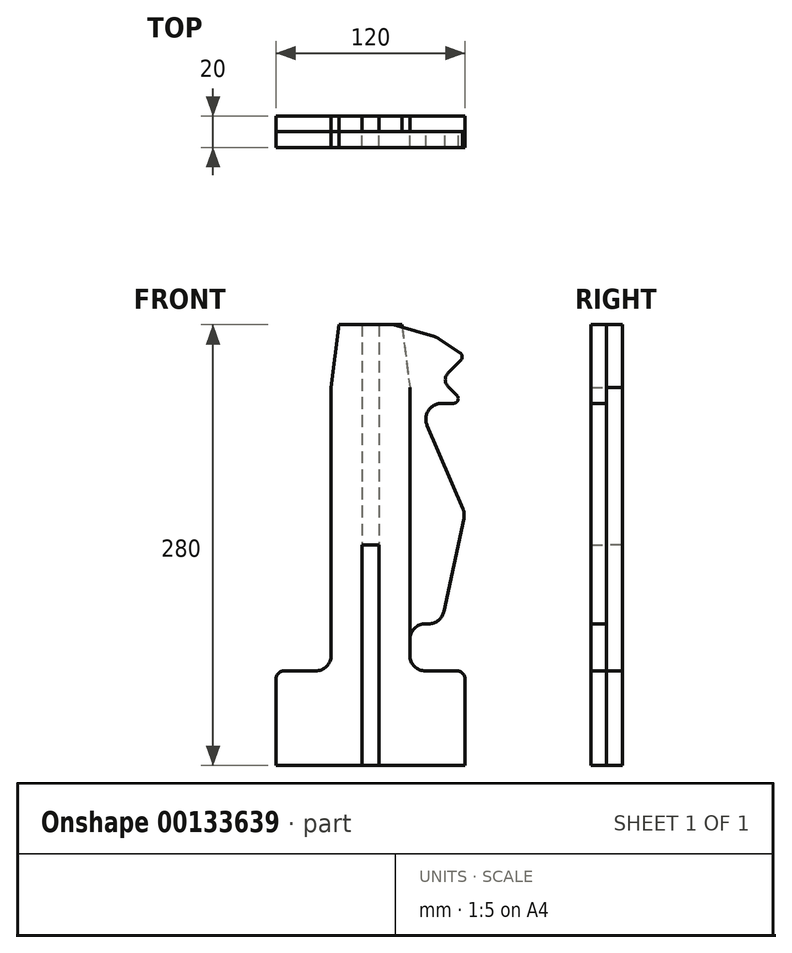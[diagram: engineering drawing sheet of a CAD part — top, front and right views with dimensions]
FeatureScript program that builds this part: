
annotation { "Feature Type Name" : "Feature", "Feature Type Description" : "" }
export const myFeature = defineFeature(function(context is Context, id is Id, definition is map)
    precondition{}
    {
        {
            var Q0;
            Q0=qCreatedBy(makeId("Front.planeOp"),FACE);
            var sketch = newSketch(context, id + "F0", { "sketchPlane" : qUnion([Q0])});
            skLineSegment(sketch, "E0.bottom", {"start": v(55, 30) * mm, "end": v(35, 30) * mm});
            skLineSegment(sketch, "E0.top", {"start": v(60, -30) * mm, "end": v(-60, -30) * mm});
            skLineSegment(sketch, "E0.left", {"start": v(60, 25) * mm, "end": v(60, -30) * mm});
            skLineSegment(sketch, "E0.right", {"start": v(-60, 25) * mm, "end": v(-60, -30) * mm});
            skPoint(sketch, "E0.middle", {"position": v(0, 0) * mm});
            skLineSegment(sketch, "E1", {"start": v(25, 40) * mm, "end": v(25, 50) * mm});
            skLineSegment(sketch, "E2", {"start": v(35, 60) * mm, "end": v(36.92, 60) * mm});
            skLineSegment(sketch, "E3", {"start": v(46.7, 67.9) * mm, "end": v(59.33, 126.89) * mm});
            skLineSegment(sketch, "E4", {"start": v(58.75, 132.92) * mm, "end": v(35.97, 186.06) * mm});
            skLineSegment(sketch, "E5", {"start": v(45.17, 200) * mm, "end": v(52.76, 200) * mm});
            skLineSegment(sketch, "E6", {"start": v(54.88, 205.12) * mm, "end": v(49.24, 210.76) * mm});
            skLineSegment(sketch, "E7", {"start": v(49.24, 219.24) * mm, "end": v(57.41, 227.41) * mm});
            skLineSegment(sketch, "E8", {"start": v(56.96, 232.03) * mm, "end": v(43.26, 241.16) * mm});
            skLineSegment(sketch, "E9", {"start": v(40.55, 242.43) * mm, "end": v(16.4, 249.59) * mm});
            skLineSegment(sketch, "E10", {"start": v(13.55, 250) * mm, "end": v(-23.38, 250) * mm});
            skLineSegment(sketch, "E11", {"start": v(-26.54, 249.49) * mm, "end": v(-40, 245) * mm});
            skLineSegment(sketch, "E12", {"start": v(-40, 245) * mm, "end": v(-55, 253) * mm});
            skLineSegment(sketch, "E13", {"start": v(-55, 253) * mm, "end": v(-50.72, 231.6) * mm});
            skLineSegment(sketch, "E14", {"start": v(-51.79, 224.79) * mm, "end": v(-57.65, 214.23) * mm});
            skLineSegment(sketch, "E15", {"start": v(-58.14, 205.53) * mm, "end": v(-37.44, 155.85) * mm});
            skLineSegment(sketch, "E16", {"start": v(-36.37, 143.82) * mm, "end": v(-52.3, 72.17) * mm});
            skLineSegment(sketch, "E17", {"start": v(-42.53, 60) * mm, "end": v(-35, 60) * mm});
            skLineSegment(sketch, "E18", {"start": v(-25, 50) * mm, "end": v(-25, 40) * mm});
            skPoint(sketch, "E19.visualSharp", {"position": v(-60, 30) * mm});
            skArc(sketch, "E19.filletArc", {"start": v(-55, 30) * mm, "mid": v(-58.54, 28.54) * mm, "end": v(-60, 25) * mm});
            skPoint(sketch, "E20.visualSharp", {"position": v(60, 30) * mm});
            skArc(sketch, "E20.filletArc", {"start": v(60, 25) * mm, "mid": v(58.54, 28.54) * mm, "end": v(55, 30) * mm});
            skPoint(sketch, "E21.visualSharp", {"position": v(-25, 60) * mm});
            skArc(sketch, "E21.filletArc", {"start": v(-25, 50) * mm, "mid": v(-27.93, 57.07) * mm, "end": v(-35, 60) * mm});
            skPoint(sketch, "E22.visualSharp", {"position": v(-55, 60) * mm});
            skArc(sketch, "E22.filletArc", {"start": v(-52.3, 72.17) * mm, "mid": v(-50.33, 63.74) * mm, "end": v(-42.53, 60) * mm});
            skPoint(sketch, "E23.visualSharp", {"position": v(45, 60) * mm});
            skArc(sketch, "E23.filletArc", {"start": v(36.92, 60) * mm, "mid": v(43.2, 62.22) * mm, "end": v(46.7, 67.9) * mm});
            skPoint(sketch, "E24.visualSharp", {"position": v(25, 60) * mm});
            skArc(sketch, "E24.filletArc", {"start": v(35, 60) * mm, "mid": v(27.93, 57.07) * mm, "end": v(25, 50) * mm});
            skPoint(sketch, "E25.newPointA", {"position": v(25, 30) * mm});
            skArc(sketch, "E25.filletArc", {"start": v(25, 40) * mm, "mid": v(27.93, 32.93) * mm, "end": v(35, 30) * mm});
            skLineSegment(sketch, "E26", {"start": v(-55, 30) * mm, "end": v(-35, 30) * mm});
            skPoint(sketch, "E27.visualSharp", {"position": v(-25, 30) * mm});
            skArc(sketch, "E27.filletArc", {"start": v(-35, 30) * mm, "mid": v(-27.93, 32.93) * mm, "end": v(-25, 40) * mm});
            skPoint(sketch, "E28.visualSharp", {"position": v(60, 130) * mm});
            skArc(sketch, "E28.filletArc", {"start": v(59.33, 126.89) * mm, "mid": v(59.5, 129.95) * mm, "end": v(58.75, 132.92) * mm});
            skPoint(sketch, "E29.visualSharp", {"position": v(30, 200) * mm});
            skArc(sketch, "E29.filletArc", {"start": v(45.17, 200) * mm, "mid": v(36.82, 195.5) * mm, "end": v(35.97, 186.06) * mm});
            skPoint(sketch, "E30.visualSharp", {"position": v(60, 200) * mm});
            skArc(sketch, "E30.filletArc", {"start": v(52.76, 200) * mm, "mid": v(55.53, 201.85) * mm, "end": v(54.88, 205.12) * mm});
            skPoint(sketch, "E31.visualSharp", {"position": v(60, 230) * mm});
            skArc(sketch, "E31.filletArc", {"start": v(57.41, 227.41) * mm, "mid": v(58.28, 229.83) * mm, "end": v(56.96, 232.03) * mm});
            skPoint(sketch, "E32.visualSharp", {"position": v(45, 215) * mm});
            skArc(sketch, "E32.filletArc", {"start": v(49.24, 219.24) * mm, "mid": v(47.49, 215) * mm, "end": v(49.24, 210.76) * mm});
            skPoint(sketch, "E33.visualSharp", {"position": v(-35, 150) * mm});
            skArc(sketch, "E33.filletArc", {"start": v(-36.37, 143.82) * mm, "mid": v(-35.98, 149.91) * mm, "end": v(-37.44, 155.85) * mm});
            skPoint(sketch, "E34.visualSharp", {"position": v(-60, 210) * mm});
            skArc(sketch, "E34.filletArc", {"start": v(-57.65, 214.23) * mm, "mid": v(-58.9, 209.94) * mm, "end": v(-58.14, 205.53) * mm});
            skPoint(sketch, "E35.visualSharp", {"position": v(-50, 228) * mm});
            skArc(sketch, "E35.filletArc", {"start": v(-51.79, 224.79) * mm, "mid": v(-50.65, 228.1) * mm, "end": v(-50.72, 231.6) * mm});
            skPoint(sketch, "E36.visualSharp", {"position": v(-25, 250) * mm});
            skArc(sketch, "E36.filletArc", {"start": v(-23.38, 250) * mm, "mid": v(-24.98, 249.87) * mm, "end": v(-26.54, 249.49) * mm});
            skPoint(sketch, "E37.visualSharp", {"position": v(15, 250) * mm});
            skArc(sketch, "E37.filletArc", {"start": v(16.4, 249.59) * mm, "mid": v(14.98, 249.9) * mm, "end": v(13.55, 250) * mm});
            skPoint(sketch, "E38.visualSharp", {"position": v(42, 242) * mm});
            skArc(sketch, "E38.filletArc", {"start": v(43.26, 241.16) * mm, "mid": v(41.95, 241.9) * mm, "end": v(40.55, 242.43) * mm});
            skLineSegment(sketch, "E39.bottom", {"start": v(-5.5, 250) * mm, "end": v(5.5, 250) * mm});
            skLineSegment(sketch, "E39.top", {"start": v(-5.5, 110) * mm, "end": v(5.5, 110) * mm});
            skLineSegment(sketch, "E39.left", {"start": v(-5.5, 250) * mm, "end": v(-5.5, 110) * mm});
            skLineSegment(sketch, "E39.right", {"start": v(5.5, 250) * mm, "end": v(5.5, 110) * mm});
            skPoint(sketch, "E39.middle", {"position": v(0, 180) * mm});
            skLineSegment(sketch, "E40.top", {"start": v(-5.5, -30) * mm, "end": v(5.5, -30) * mm});
            skLineSegment(sketch, "E40.left", {"start": v(-5.5, 110) * mm, "end": v(-5.5, -30) * mm});
            skLineSegment(sketch, "E40.right", {"start": v(5.5, 110) * mm, "end": v(5.5, -30) * mm});
            skPoint(sketch, "E40.middle", {"position": v(0, 40) * mm});
            skLineSegment(sketch, "E41", {"start": v(-25, 40) * mm, "end": v(-25, 210) * mm});
            skLineSegment(sketch, "E42", {"start": v(-25, 210) * mm, "end": v(-20, 250) * mm});
            skLineSegment(sketch, "E43", {"start": v(-20, 250) * mm, "end": v(20, 250) * mm});
            skLineSegment(sketch, "E44", {"start": v(20, 250) * mm, "end": v(25, 210) * mm});
            skLineSegment(sketch, "E45", {"start": v(25, 210) * mm, "end": v(25, 40) * mm});
            skSolve(sketch);
        }
        {
            var Q0;
            Q0=makeQuery(id+"F0.imprint","IMPRINT",FACE,{"disambiguationData":[TD([[makeQuery(id+"F0.imprint","IMPRINT",EDGE,{"derivedFrom":sQuery(id+"F0.wireOp",EDGE,"E2")}),1.0]])]});
            var Q1;
            Q1=makeQuery(id+"F0.imprint","IMPRINT",FACE,{"disambiguationData":[TD([[makeQuery(id+"F0.imprint","IMPRINT",EDGE,{"derivedFrom":sQuery(id+"F0.wireOp",EDGE,"E10")}),1.0]])]});
            var Q2;
            {var subQ6=sQuery(id+"F0.wireOp",EDGE,"E0.right");Q2=makeQuery(id+"F0.imprint","IMPRINT",FACE,{"disambiguationData":[TD([[makeQuery(id+"F0.imprint","IMPRINT",EDGE,{"derivedFrom":subQ6}),1.0]])]});}
            var Q3;
            {var subQ0=sQuery(id+"F0.wireOp",EDGE,"E39.left");Q3=makeQuery(id+"F0.imprint","IMPRINT",FACE,{"disambiguationData":[TD([[makeQuery(id+"F0.imprint","IMPRINT",EDGE,{"derivedFrom":subQ0}),1.0]])]});}
            var Q4;
            Q4=makeQuery(id+"F0.imprint","IMPRINT",FACE,{"disambiguationData":[TD([[makeQuery(id+"F0.imprint","IMPRINT",EDGE,{"derivedFrom":sQuery(id+"F0.wireOp",EDGE,"E0.bottom")}),1.0]])]});
            extrude(context, id + "F1", {"entities" : qUnion([Q0, Q1, Q2, Q3, Q4]), "depth" : 10 * mm});
        }
        {
            var Q0;
            {var subQ6=sQuery(id+"F0.wireOp",EDGE,"E0.right");Q0=makeQuery(id+"F0.imprint","IMPRINT",FACE,{"disambiguationData":[TD([[makeQuery(id+"F0.imprint","IMPRINT",EDGE,{"derivedFrom":subQ6}),1.0]])]});}
            var Q1;
            Q1=makeQuery(id+"F0.imprint","IMPRINT",FACE,{"disambiguationData":[TD([[makeQuery(id+"F0.imprint","IMPRINT",EDGE,{"derivedFrom":sQuery(id+"F0.wireOp",EDGE,"E0.bottom")}),1.0]])]});
            var Q2;
            Q2=makeQuery(id+"F0.imprint","IMPRINT",FACE,{"disambiguationData":[TD([[makeQuery(id+"F0.imprint","IMPRINT",EDGE,{"derivedFrom":sQuery(id+"F0.wireOp",EDGE,"E39.top")}),-1.0]])]});
            var Q3;
            {var subQ0=sQuery(id+"F0.wireOp",EDGE,"E37.filletArc");Q3=makeQuery(id+"F0.imprint","IMPRINT",FACE,{"disambiguationData":[TD([[makeQuery(id+"F0.imprint","IMPRINT",EDGE,{"derivedFrom":subQ0}),-1.0]])]});}
            extrude(context, id + "F2", {"entities" : qUnion([Q0, Q1, Q2, Q3]), "oppositeDirection" : true, "depth" : 10 * mm});
        }
    });
